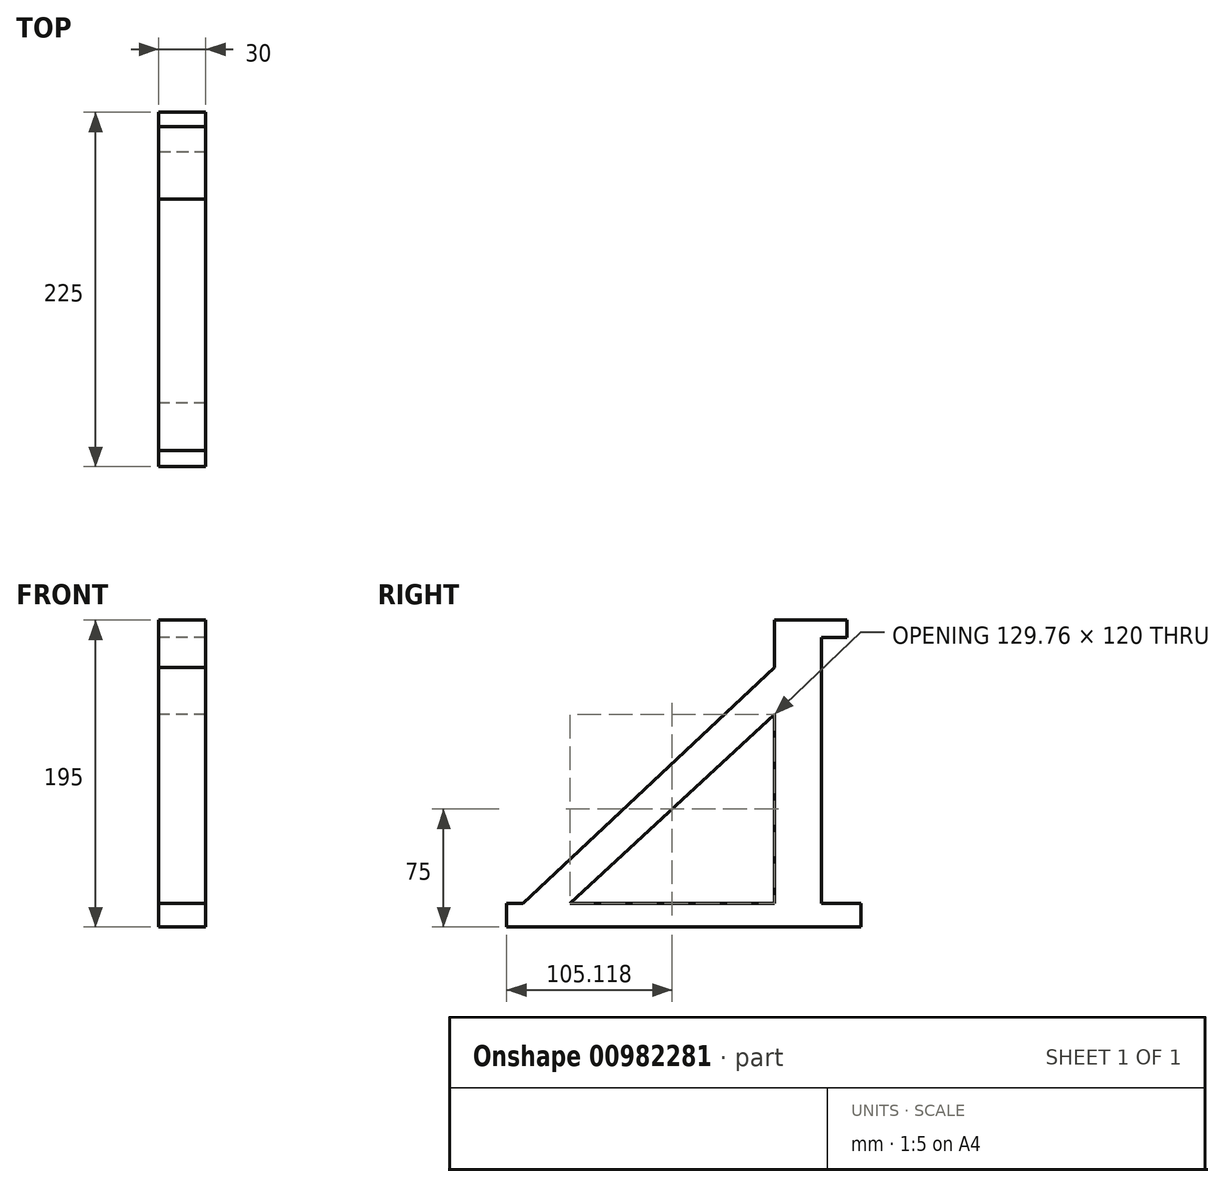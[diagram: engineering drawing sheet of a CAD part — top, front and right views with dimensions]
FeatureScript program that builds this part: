
annotation { "Feature Type Name" : "Feature", "Feature Type Description" : "" }
export const myFeature = defineFeature(function(context is Context, id is Id, definition is map)
    precondition{}
    {
        {
            var Q0;
            Q0=qCreatedBy(makeId("Top.planeOp"),FACE);
            var sketch = newSketch(context, id + "F0", { "sketchPlane" : qUnion([Q0])});
            skLineSegment(sketch, "E0.bottom", {"start": v(-15, 25) * mm, "end": v(15, 25) * mm});
            skLineSegment(sketch, "E0.top", {"start": v(-15, -25) * mm, "end": v(15, -25) * mm});
            skLineSegment(sketch, "E0.left", {"start": v(-15, 25) * mm, "end": v(-15, -25) * mm});
            skLineSegment(sketch, "E0.right", {"start": v(15, 25) * mm, "end": v(15, -25) * mm});
            skPoint(sketch, "E0.middle", {"position": v(0, 0) * mm});
            skSolve(sketch);
        }
        {
            var Q0;
            Q0 = qSketchRegion(id + "F0", true);
            extrude(context, id + "F1", {"entities" : qUnion([Q0]), "depth" : 15 * mm, "offsetDistance" : 25 * mm});
        }
        {
            var Q0;
            Q0=makeQuery(id+"F1.opExtrude","CAP_FACE",FACE,{"disambiguationData":[OSD([sQuery(id+"F0.wireOp",EDGE,"E0.bottom"),sQuery(id+"F0.wireOp",EDGE,"E0.top"),sQuery(id+"F0.wireOp",EDGE,"E0.left"),sQuery(id+"F0.wireOp",EDGE,"E0.right")])],"isStart":false});
            var sketch = newSketch(context, id + "F2", { "sketchPlane" : qUnion([Q0])});
            skLineSegment(sketch, "E1.bottom", {"start": v(-15, 15) * mm, "end": v(15, 15) * mm});
            skLineSegment(sketch, "E1.top", {"start": v(-15, -15) * mm, "end": v(15, -15) * mm});
            skLineSegment(sketch, "E1.left", {"start": v(-15, 15) * mm, "end": v(-15, -15) * mm});
            skLineSegment(sketch, "E1.right", {"start": v(15, 15) * mm, "end": v(15, -15) * mm});
            skPoint(sketch, "E1.middle", {"position": v(0, 0) * mm});
            skSolve(sketch);
        }
        {
            var Q0;
            Q0=makeQuery(id+"F2.imprint","IMPRINT",FACE,{"disambiguationData":[TD([[makeQuery(id+"F2.imprint","IMPRINT",EDGE,{"derivedFrom":sQuery(id+"F2.wireOp",EDGE,"E1.bottom")}),-1.0]])]});
            extrude(context, id + "F3", {"entities" : qUnion([Q0]), "operationType" : NewBodyOperationType.ADD, "depth" : 150 * mm, "offsetDistance" : 25 * mm});
        }
        {
            var Q0;
            Q0=makeQuery(id+"F1.opExtrude","SWEPT_FACE",FACE,{"disambiguationData":[OSD([sQuery(id+"F0.wireOp",EDGE,"E0.top")])]});
            extrude(context, id + "F4", {"entities" : qUnion([Q0]), "operationType" : NewBodyOperationType.ADD, "depth" : 160 * mm, "offsetDistance" : 25 * mm});
        }
        {
            var Q0;
            {var subQ0=sQuery(id+"F0.wireOp",EDGE,"E0.left");Q0=makeQuery(id+"F4.boolean.opBoolean","MERGE",FACE,{"derivedFrom":[makeQuery(id+"F3.boolean.opBoolean","MERGE",FACE,{"derivedFrom":[makeQuery(id+"F1.opExtrude","SWEPT_FACE",FACE,{"disambiguationData":[OSD([subQ0])]}),makeQuery(id+"F3.opExtrude","SWEPT_FACE",FACE,{"disambiguationData":[OSD([sQuery(id+"F2.wireOp",EDGE,"E1.left")])]})]}),makeQuery(id+"F4.opExtrude","SWEPT_FACE",FACE,{"disambiguationData":[OSD([sQuery(id+"F0.wireOp",EDGE,"E0.top"),subQ0])]})]});}
            var sketch = newSketch(context, id + "F5", { "sketchPlane" : qUnion([Q0])});
            skLineSegment(sketch, "E2", {"start": v(174.76, 15) * mm, "end": v(15, 165) * mm});
            skLineSegment(sketch, "E3", {"start": v(15, 165) * mm, "end": v(15, 135) * mm});
            skLineSegment(sketch, "E4", {"start": v(174.76, 15) * mm, "end": v(144.76, 15) * mm});
            skLineSegment(sketch, "E5", {"start": v(144.76, 15) * mm, "end": v(15, 135) * mm});
            skSolve(sketch);
        }
        {
            var Q0;
            Q0 = qSketchRegion(id + "F5", true);
            extrude(context, id + "F6", {"entities" : qUnion([Q0]), "operationType" : NewBodyOperationType.ADD, "depth" : -30 * mm, "offsetDistance" : 25 * mm});
        }
        {
            var Q0;
            {var subQ0=sQuery(id+"F0.wireOp",EDGE,"E0.left");Q0=makeQuery(id+"F6.boolean.opBoolean","MERGE",FACE,{"derivedFrom":[makeQuery(id+"F4.boolean.opBoolean","MERGE",FACE,{"derivedFrom":[makeQuery(id+"F3.boolean.opBoolean","MERGE",FACE,{"derivedFrom":[makeQuery(id+"F1.opExtrude","SWEPT_FACE",FACE,{"disambiguationData":[OSD([subQ0])]}),makeQuery(id+"F3.opExtrude","SWEPT_FACE",FACE,{"disambiguationData":[OSD([sQuery(id+"F2.wireOp",EDGE,"E1.left")])]})]}),makeQuery(id+"F4.opExtrude","SWEPT_FACE",FACE,{"disambiguationData":[OSD([sQuery(id+"F0.wireOp",EDGE,"E0.top"),subQ0])]})]}),makeQuery(id+"F6.opExtrude","CAP_FACE",FACE,{"disambiguationData":[OSD([sQuery(id+"F5.wireOp",EDGE,"E2"),sQuery(id+"F5.wireOp",EDGE,"E3"),sQuery(id+"F5.wireOp",EDGE,"E4"),sQuery(id+"F5.wireOp",EDGE,"E5")])],"isStart":true})]});}
            var sketch = newSketch(context, id + "F7", { "sketchPlane" : qUnion([Q0])});
            skLineSegment(sketch, "E6.bottom", {"start": v(-15, 165) * mm, "end": v(15, 165) * mm});
            skLineSegment(sketch, "E6.top", {"start": v(-15, 195) * mm, "end": v(15, 195) * mm});
            skLineSegment(sketch, "E6.left", {"start": v(-15, 165) * mm, "end": v(-15, 195) * mm});
            skLineSegment(sketch, "E6.right", {"start": v(15, 165) * mm, "end": v(15, 195) * mm});
            skLineSegment(sketch, "E7.bottom", {"start": v(-15, 195) * mm, "end": v(-31, 195) * mm});
            skLineSegment(sketch, "E7.top", {"start": v(-15, 189) * mm, "end": v(-31, 189) * mm});
            skLineSegment(sketch, "E7.left", {"start": v(-15, 195) * mm, "end": v(-15, 189) * mm});
            skLineSegment(sketch, "E7.right", {"start": v(-31, 195) * mm, "end": v(-31, 189) * mm});
            skSolve(sketch);
        }
        {
            var Q0;
            Q0=makeQuery(id+"F7.imprint","IMPRINT",FACE,{"disambiguationData":[TD([[makeQuery(id+"F7.imprint","IMPRINT",EDGE,{"derivedFrom":sQuery(id+"F7.wireOp",EDGE,"E6.bottom")}),1.0]])]});
            var Q1;
            Q1=makeQuery(id+"F7.imprint","IMPRINT",FACE,{"disambiguationData":[TD([[makeQuery(id+"F7.imprint","IMPRINT",EDGE,{"derivedFrom":sQuery(id+"F7.wireOp",EDGE,"E7.bottom")}),1.0]])]});
            extrude(context, id + "F8", {"entities" : qUnion([Q0, Q1]), "operationType" : NewBodyOperationType.ADD, "depth" : -30 * mm, "offsetDistance" : 25 * mm});
        }
        {
            var Q0;
            Q0=makeQuery(id+"F1.opExtrude","SWEPT_FACE",FACE,{"disambiguationData":[OSD([sQuery(id+"F0.wireOp",EDGE,"E0.bottom")])]});
            extrude(context, id + "F9", {"entities" : qUnion([Q0]), "operationType" : NewBodyOperationType.ADD, "depth" : 15 * mm, "offsetDistance" : 25 * mm});
        }
        {
            var Q0;
            Q0=makeQuery(id+"F8.opExtrude","SWEPT_FACE",FACE,{"disambiguationData":[OSD([sQuery(id+"F7.wireOp",EDGE,"E7.top")])]});
            extrude(context, id + "F10", {"entities" : qUnion([Q0]), "operationType" : NewBodyOperationType.ADD, "depth" : 5 * mm, "offsetDistance" : 25 * mm});
        }
    });
